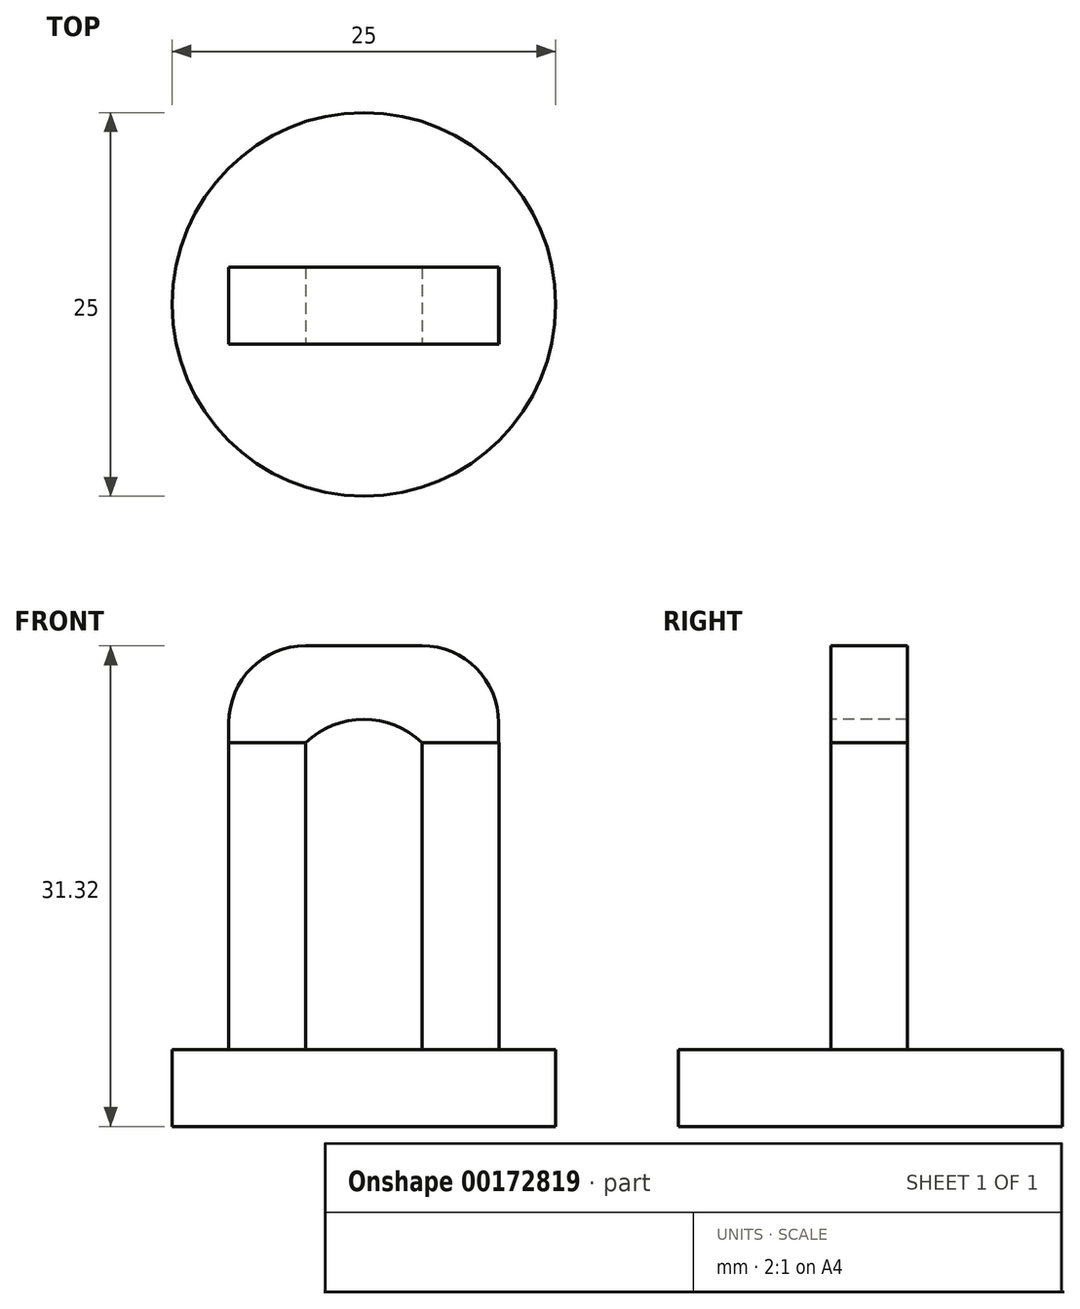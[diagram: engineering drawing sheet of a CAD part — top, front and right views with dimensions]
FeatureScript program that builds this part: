
annotation { "Feature Type Name" : "Feature", "Feature Type Description" : "" }
export const myFeature = defineFeature(function(context is Context, id is Id, definition is map)
    precondition{}
    {
        {
            var Q0;
            Q0=qCreatedBy(makeId("Top.planeOp"),FACE);
            var sketch = newSketch(context, id + "F0", { "sketchPlane" : qUnion([Q0])});
            skCircle(sketch, "E0", {"center": v(0, 0) * mm, "radius": 12.5 * mm});
            skSolve(sketch);
        }
        {
            var Q0;
            Q0 = qSketchRegion(id + "F0", true);
            extrude(context, id + "F1", {"entities" : qUnion([Q0]), "depth" : 5 * mm});
        }
        {
            var Q0;
            Q0=makeQuery(id+"F1.opExtrude","CAP_FACE",FACE,{"disambiguationData":[OSD([sQuery(id+"F0.wireOp",EDGE,"E0")])],"isStart":false});
            var sketch = newSketch(context, id + "F2", { "sketchPlane" : qUnion([Q0])});
            skLineSegment(sketch, "E1.bottom", {"start": v(-8.8, 2.42) * mm, "end": v(-3.8, 2.42) * mm});
            skLineSegment(sketch, "E1.top", {"start": v(-8.8, -2.58) * mm, "end": v(-3.8, -2.58) * mm});
            skLineSegment(sketch, "E1.left", {"start": v(-8.8, 2.42) * mm, "end": v(-8.8, -2.58) * mm});
            skLineSegment(sketch, "E1.right", {"start": v(-3.8, 2.42) * mm, "end": v(-3.8, -2.58) * mm});
            skLineSegment(sketch, "E2.MirrorCS", {"start": v(8.8, 2.42) * mm, "end": v(8.8, -2.58) * mm});
            skLineSegment(sketch, "E3.MirrorCS", {"start": v(8.8, 2.42) * mm, "end": v(3.8, 2.42) * mm});
            skLineSegment(sketch, "E4.MirrorCS", {"start": v(3.8, 2.42) * mm, "end": v(3.8, -2.58) * mm});
            skLineSegment(sketch, "E5.MirrorCS", {"start": v(8.8, -2.58) * mm, "end": v(3.8, -2.58) * mm});
            skSolve(sketch);
        }
        {
            var Q0;
            Q0 = qSketchRegion(id + "F2", true);
            extrude(context, id + "F3", {"entities" : qUnion([Q0]), "operationType" : NewBodyOperationType.ADD, "depth" : 20 * mm});
        }
        {
            var Q0;
            Q0=makeQuery(id+"F3.opExtrude","SWEPT_FACE",FACE,{"disambiguationData":[OSD([sQuery(id+"F2.wireOp",EDGE,"E1.top")])]});
            var sketch = newSketch(context, id + "F4", { "sketchPlane" : qUnion([Q0])});
            skLineSegment(sketch, "E6.bottom", {"start": v(-8.8, 25) * mm, "end": v(-3.8, 25) * mm});
            skLineSegment(sketch, "E6.top", {"start": v(-8.8, 31.32) * mm, "end": v(8.79, 31.32) * mm});
            skLineSegment(sketch, "E6.left", {"start": v(-8.8, 25) * mm, "end": v(-8.8, 31.32) * mm});
            skLineSegment(sketch, "E6.right", {"start": v(8.79, 25) * mm, "end": v(8.79, 31.32) * mm});
            skArc(sketch, "E7", {"start": v(3.8, 25) * mm, "mid": v(0, 26.52) * mm, "end": v(-3.8, 25) * mm});
            skLineSegment(sketch, "E8.trimOffspring", {"start": v(3.8, 25) * mm, "end": v(8.79, 25) * mm});
            skSolve(sketch);
        }
        {
            var Q0;
            Q0 = qSketchRegion(id + "F4", true);
            extrude(context, id + "F5", {"entities" : qUnion([Q0]), "oppositeDirection" : true, "depth" : 5 * mm});
        }
        {
            var Q0;
            Q0=makeQuery(id+"F5.opExtrude","SWEPT_EDGE",EDGE,{"disambiguationData":[OSD([sQuery(id+"F4.wireOp",EDGE,"E6.top"),sQuery(id+"F4.wireOp",EDGE,"E6.right")])]});
            var Q1;
            Q1=makeQuery(id+"F5.opExtrude","SWEPT_EDGE",EDGE,{"disambiguationData":[OSD([sQuery(id+"F4.wireOp",EDGE,"E6.top"),sQuery(id+"F4.wireOp",EDGE,"E6.left")])]});
            fillet(context, id + "F6", {"entities" : qUnion([Q0, Q1]), "radius" : 5 * mm, "tangentPropagation" : true, "allowEdgeOverflow" : false});
        }
    });
